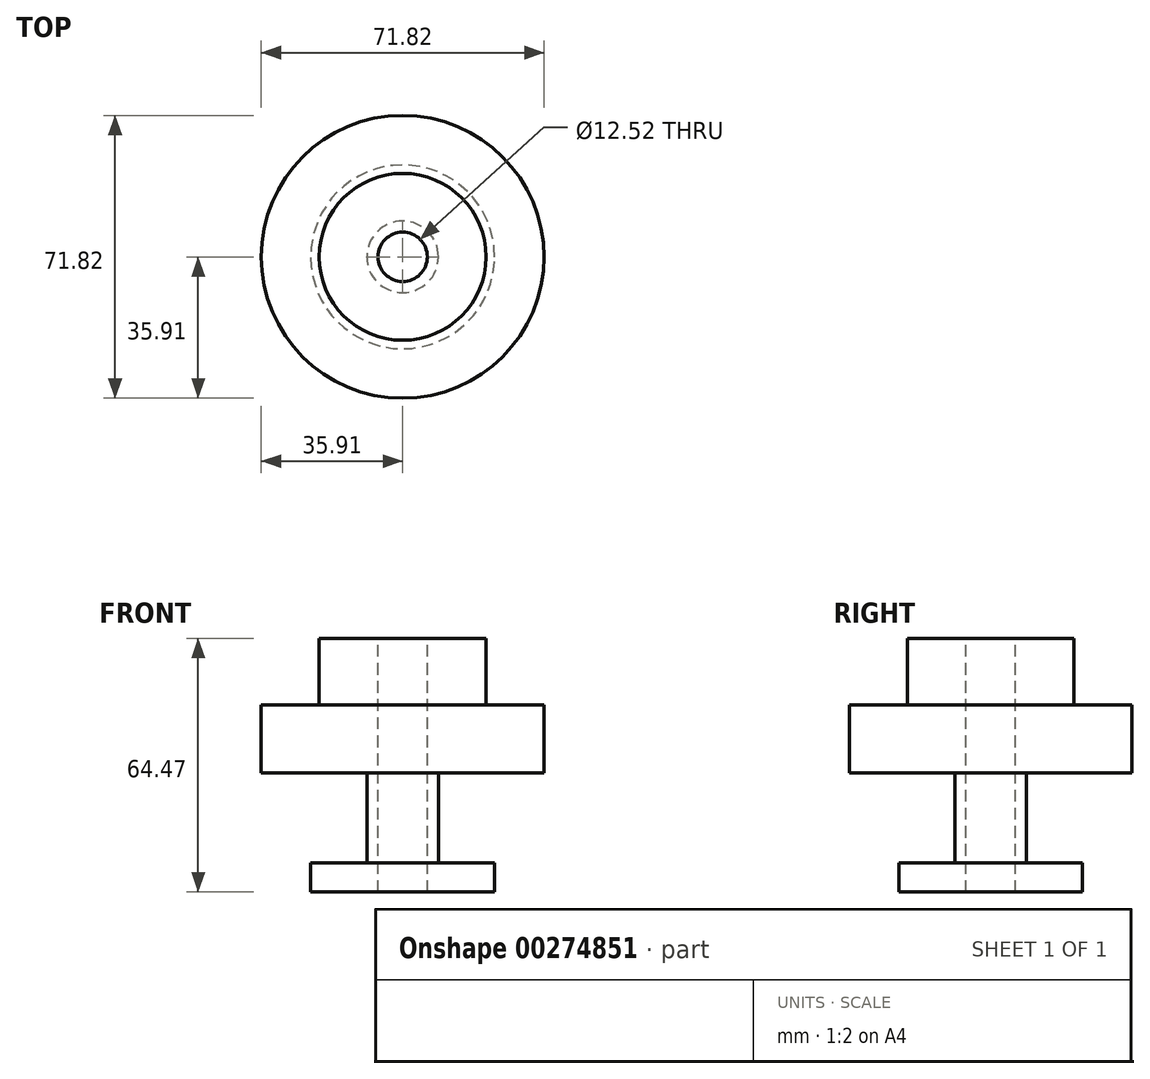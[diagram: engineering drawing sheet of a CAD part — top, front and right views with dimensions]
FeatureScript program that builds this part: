
annotation { "Feature Type Name" : "Feature", "Feature Type Description" : "" }
export const myFeature = defineFeature(function(context is Context, id is Id, definition is map)
    precondition{}
    {
        {
            var Q0;
            Q0=qCreatedBy(makeId("Front.planeOp"),FACE);
            var sketch = newSketch(context, id + "F0", { "sketchPlane" : qUnion([Q0])});
            skLineSegment(sketch, "E0", {"start": v(-21.2, 38.5) * mm, "end": v(-21.2, 21.63) * mm});
            skLineSegment(sketch, "E1", {"start": v(-21.2, 21.63) * mm, "end": v(-35.91, 21.63) * mm});
            skLineSegment(sketch, "E2", {"start": v(-35.91, 21.63) * mm, "end": v(-35.91, 4.33) * mm});
            skLineSegment(sketch, "E3", {"start": v(-35.91, 4.33) * mm, "end": v(-9.09, 4.33) * mm});
            skLineSegment(sketch, "E4", {"start": v(-9.09, 4.33) * mm, "end": v(-9.09, -18.6) * mm});
            skLineSegment(sketch, "E5", {"start": v(-9.09, -18.6) * mm, "end": v(-23.37, -18.6) * mm});
            skLineSegment(sketch, "E6", {"start": v(-23.37, -18.6) * mm, "end": v(-23.37, -25.96) * mm});
            skLineSegment(sketch, "E7", {"start": v(-21.2, 38.5) * mm, "end": v(-6.26, 38.5) * mm});
            skLineSegment(sketch, "E8", {"start": v(-6.26, 38.5) * mm, "end": v(-6.26, -25.96) * mm});
            skLineSegment(sketch, "E9", {"start": v(-6.26, -25.96) * mm, "end": v(-23.37, -25.96) * mm});
            skLineSegment(sketch, "E10", {"start": v(0, 38.77) * mm, "end": v(0, -26.4) * mm, "construction": true});
            skSolve(sketch);
        }
        {
            var Q0;
            Q0=makeQuery(id+"F0.imprint","IMPRINT",FACE,{"disambiguationData":[TD([[makeQuery(id+"F0.imprint","IMPRINT",EDGE,{"derivedFrom":sQuery(id+"F0.wireOp",EDGE,"E0")}),1.0]])]});
            var Q1;
            Q1=sQuery(id+"F0.wireOp",EDGE,"E10");
            revolve(context, id + "F1", {"entities" : qUnion([Q0]), "axis" : qUnion([Q1]), "revolveType" : RevolveType.FULL});
        }
    });
